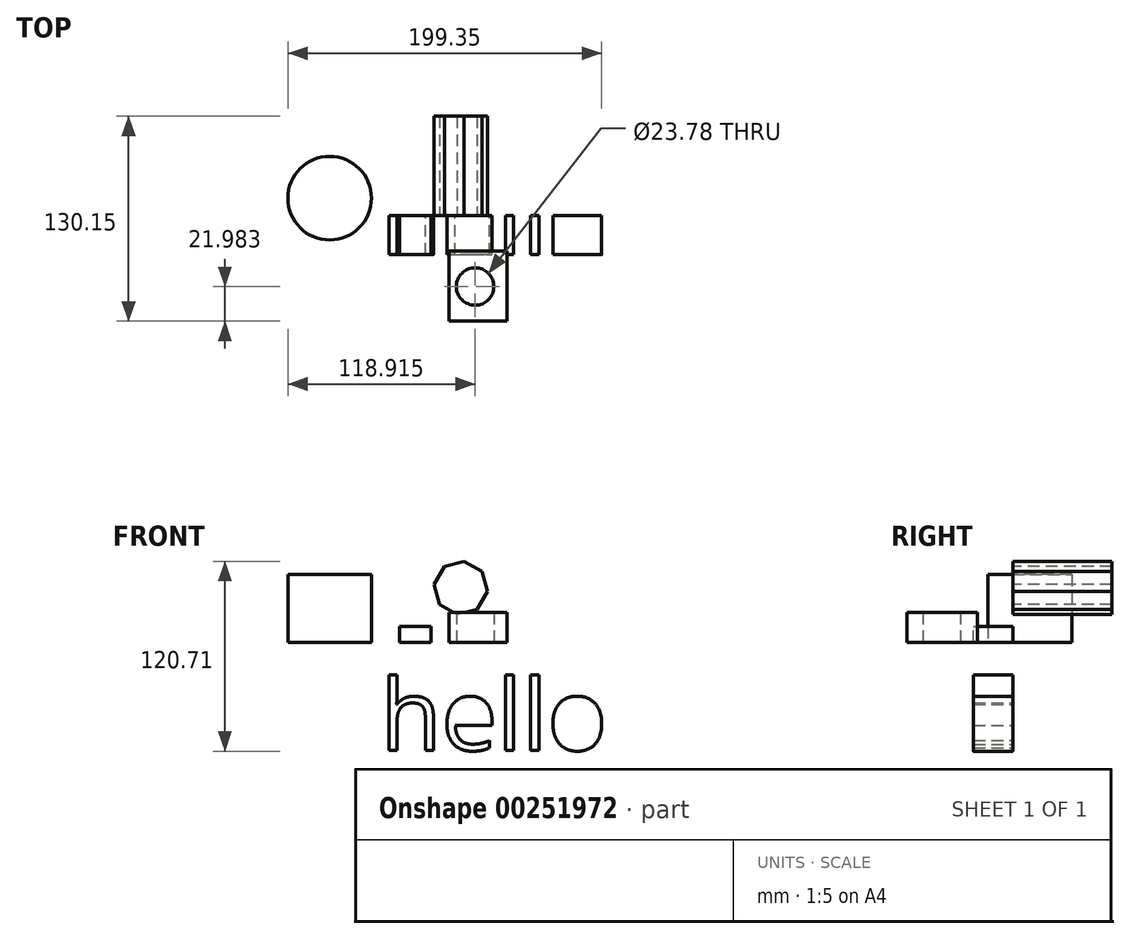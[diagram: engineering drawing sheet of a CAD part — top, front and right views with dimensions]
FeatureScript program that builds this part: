
annotation { "Feature Type Name" : "Feature", "Feature Type Description" : "" }
export const myFeature = defineFeature(function(context is Context, id is Id, definition is map)
    precondition{}
    {
        {
            var Q0;
            Q0=qCreatedBy(makeId("Front.planeOp"),FACE);
            var sketch = newSketch(context, id + "F0", { "sketchPlane" : qUnion([Q0])});
            skLineSegment(sketch, "E0.bottom", {"start": v(0, 0) * mm, "end": v(20, 0) * mm});
            skLineSegment(sketch, "E0.top", {"start": v(0, 10) * mm, "end": v(20, 10) * mm});
            skLineSegment(sketch, "E0.left", {"start": v(0, 0) * mm, "end": v(0, 10) * mm});
            skLineSegment(sketch, "E0.right", {"start": v(20, 0) * mm, "end": v(20, 10) * mm});
            skSolve(sketch);
        }
        {
            var Q0;
            Q0=makeQuery(id+"F0.imprint","IMPRINT",FACE,{"disambiguationData":[TD([[makeQuery(id+"F0.imprint","IMPRINT",EDGE,{"derivedFrom":sQuery(id+"F0.wireOp",EDGE,"E0.bottom")}),1.0]])]});
            extrude(context, id + "F1", {"entities" : qUnion([Q0]), "depth" : 25 * mm});
        }
        {
            var Q0;
            Q0=qCreatedBy(makeId("Top.planeOp"),FACE);
            var sketch = newSketch(context, id + "F2", { "sketchPlane" : qUnion([Q0])});
            skCircle(sketch, "E1", {"center": v(-44.36, 10.95) * mm, "radius": 26.55 * mm});
            skSolve(sketch);
        }
        {
            var Q0;
            Q0=makeQuery(id+"F2.imprint","IMPRINT",FACE,{"disambiguationData":[TD([[makeQuery(id+"F2.imprint","IMPRINT",EDGE,{"derivedFrom":sQuery(id+"F2.wireOp",EDGE,"E1")}),1.0]])]});
            extrude(context, id + "F3", {"entities" : qUnion([Q0]), "depth" : 43 * mm});
        }
        {
            var Q0;
            Q0=qCreatedBy(makeId("Front.planeOp"),FACE);
            var sketch = newSketch(context, id + "F4", { "sketchPlane" : qUnion([Q0])});
            skCircle(sketch, "E2.cCircle", {"center": v(38.83, 34.61) * mm, "radius": 15.77 * mm, "construction": true});
            skLineSegment(sketch, "E2.0", {"start": v(55.75, 32.38) * mm, "end": v(49.2, 21.07) * mm});
            skLineSegment(sketch, "E2.1", {"start": v(49.2, 21.07) * mm, "end": v(36.59, 17.7) * mm});
            skLineSegment(sketch, "E2.2", {"start": v(36.59, 17.7) * mm, "end": v(25.28, 24.23) * mm});
            skLineSegment(sketch, "E2.3", {"start": v(25.28, 24.23) * mm, "end": v(21.9, 36.85) * mm});
            skLineSegment(sketch, "E2.4", {"start": v(21.9, 36.85) * mm, "end": v(28.44, 48.16) * mm});
            skLineSegment(sketch, "E2.5", {"start": v(28.44, 48.16) * mm, "end": v(41.06, 51.54) * mm});
            skLineSegment(sketch, "E2.6", {"start": v(41.06, 51.54) * mm, "end": v(52.37, 45) * mm});
            skLineSegment(sketch, "E2.7", {"start": v(52.37, 45) * mm, "end": v(55.75, 32.38) * mm});
            skPoint(sketch, "E2.0.midPoint", {"position": v(52.48, 26.72) * mm});
            skSolve(sketch);
        }
        {
            var Q0;
            Q0=makeQuery(id+"F4.imprint","IMPRINT",FACE,{"disambiguationData":[TD([[makeQuery(id+"F4.imprint","IMPRINT",EDGE,{"derivedFrom":sQuery(id+"F4.wireOp",EDGE,"E2.0")}),-1.0]])]});
            extrude(context, id + "F5", {"entities" : qUnion([Q0]), "oppositeDirection" : true, "depth" : 63 * mm});
        }
        {
            var Q0;
            Q0=qCreatedBy(makeId("Top.planeOp"),FACE);
            var sketch = newSketch(context, id + "F6", { "sketchPlane" : qUnion([Q0])});
            skLineSegment(sketch, "E3.bottom", {"start": v(31.32, -22.56) * mm, "end": v(68.27, -22.56) * mm});
            skLineSegment(sketch, "E3.top", {"start": v(31.32, -67.15) * mm, "end": v(68.27, -67.15) * mm});
            skLineSegment(sketch, "E3.left", {"start": v(31.32, -22.56) * mm, "end": v(31.32, -67.15) * mm});
            skLineSegment(sketch, "E3.right", {"start": v(68.27, -22.56) * mm, "end": v(68.27, -67.15) * mm});
            skCircle(sketch, "E4", {"center": v(48, -45.17) * mm, "radius": 11.89 * mm});
            skSolve(sketch);
        }
        {
            var Q0;
            Q0=makeQuery(id+"F6.imprint","IMPRINT",FACE,{"disambiguationData":[TD([[makeQuery(id+"F6.imprint","IMPRINT",EDGE,{"derivedFrom":sQuery(id+"F6.wireOp",EDGE,"E3.bottom")}),-1.0]])]});
            extrude(context, id + "F7", {"entities" : qUnion([Q0]), "depth" : 19 * mm});
        }
        {
            var Q0;
            Q0=qCreatedBy(makeId("Top.planeOp"),FACE);
            var sketch = newSketch(context, id + "F8", { "sketchPlane" : qUnion([Q0])});
            skArc(sketch, "E5", {"start": v(-44.09, -64.45) * mm, "mid": v(-30.16, -46.97) * mm, "end": v(-50.3, -37.28) * mm});
            skSolve(sketch);
        }
        {
            var Q0;
            Q0=sQuery(id+"F8.wireOp",EDGE,"E5");
            extrude(context, id + "F9", {"bodyType" : ToolBodyType.SURFACE, "surfaceEntities" : qUnion([Q0]), "depth" : 16 * mm});
        }
        {
            var Q0;
            Q0=qCreatedBy(makeId("Front.planeOp"),FACE);
            var sketch = newSketch(context, id + "F10", { "sketchPlane" : qUnion([Q0])});
            skText(sketch, "E6", { "text": "hello", "fontName": "OpenSans-Regular.ttf"});
            const initialGuessF10  = {"E6": [-0.01216, -0.06855, 1, 0, 0.04542]};
            skSetInitialGuess(sketch, initialGuessF10);
            skSolve(sketch);
        }
        {
            var Q0;
            Q0 = qSketchRegion(id + "F10", true);
            var Q1;
            Q1=makeQuery(id+"F10.imprint","IMPRINT",FACE,{"disambiguationData":[TD([[makeQuery(id+"F10.imprint","IMPRINT",EDGE,{"derivedFrom":sQuery(id+"F10.wireOp",EDGE,"E6.sketch_text.stroke-0")}),-1.0]])]});
            var Q2;
            Q2=makeQuery(id+"F10.imprint","IMPRINT",FACE,{"disambiguationData":[TD([[makeQuery(id+"F10.imprint","IMPRINT",EDGE,{"derivedFrom":sQuery(id+"F10.wireOp",EDGE,"E6.sketch_text.stroke-54")}),1.0]])]});
            var Q3;
            Q3=makeQuery(id+"F10.imprint","IMPRINT",FACE,{"disambiguationData":[TD([[makeQuery(id+"F10.imprint","IMPRINT",EDGE,{"derivedFrom":sQuery(id+"F10.wireOp",EDGE,"E6.sketch_text.stroke-37")}),-1.0]])]});
            var Q4;
            Q4=makeQuery(id+"F10.imprint","IMPRINT",FACE,{"disambiguationData":[TD([[makeQuery(id+"F10.imprint","IMPRINT",EDGE,{"derivedFrom":sQuery(id+"F10.wireOp",EDGE,"E6.sketch_text.stroke-41")}),-1.0]])]});
            var Q5;
            Q5=makeQuery(id+"F10.imprint","IMPRINT",FACE,{"disambiguationData":[TD([[makeQuery(id+"F10.imprint","IMPRINT",EDGE,{"derivedFrom":sQuery(id+"F10.wireOp",EDGE,"E6.sketch_text.stroke-18")}),-1.0]])]});
            var Q6;
            Q6=makeQuery(id+"F10.imprint","IMPRINT",FACE,{"disambiguationData":[TD([[makeQuery(id+"F10.imprint","IMPRINT",EDGE,{"derivedFrom":sQuery(id+"F10.wireOp",EDGE,"E6.sketch_text.stroke-32")}),1.0]])]});
            var Q7;
            Q7=makeQuery(id+"F10.imprint","IMPRINT",FACE,{"disambiguationData":[TD([[makeQuery(id+"F10.imprint","IMPRINT",EDGE,{"derivedFrom":sQuery(id+"F10.wireOp",EDGE,"E6.sketch_text.stroke-45")}),-1.0]])]});
            extrude(context, id + "F11", {"entities" : qUnion([Q0, Q1, Q2, Q3, Q4, Q5, Q6, Q7]), "depth" : 25 * mm});
        }
    });
